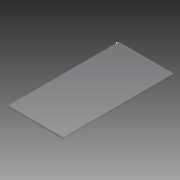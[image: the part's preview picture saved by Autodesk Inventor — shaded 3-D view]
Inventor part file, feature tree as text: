
AUTODESK INVENTOR PART (.ipt)
format: ipt  version: 2015 (Build 190159000, 159)  size: 93,184 bytes
history: native  units: in
note: dims shown in document units (in); Inventor stores cm internally (conversion verified against a paired STEP export)
features: sketch x3, extrude x2
ambient origin geometry x8: Origin, YZ Plane, XZ Plane, XY Plane, X Axis, Y Axis, Z Axis, Center Point
bodies: Solid1 (feature_tree)
feature tree (5):
  sketch  "Sketch1"  dims[d0=8.622in d1=0.2756in]
  extrude  "Extrusion1"  Depth=0.2756in
  extrude  "Extrusion3"  Depth=16.6929in
  sketch  "Sketch2"  dims[d2=16.6929in d3=0.0in d7=0.2524in]
  sketch  "Sketch4"  dims[d8=22.7313in d9=0.0in]
